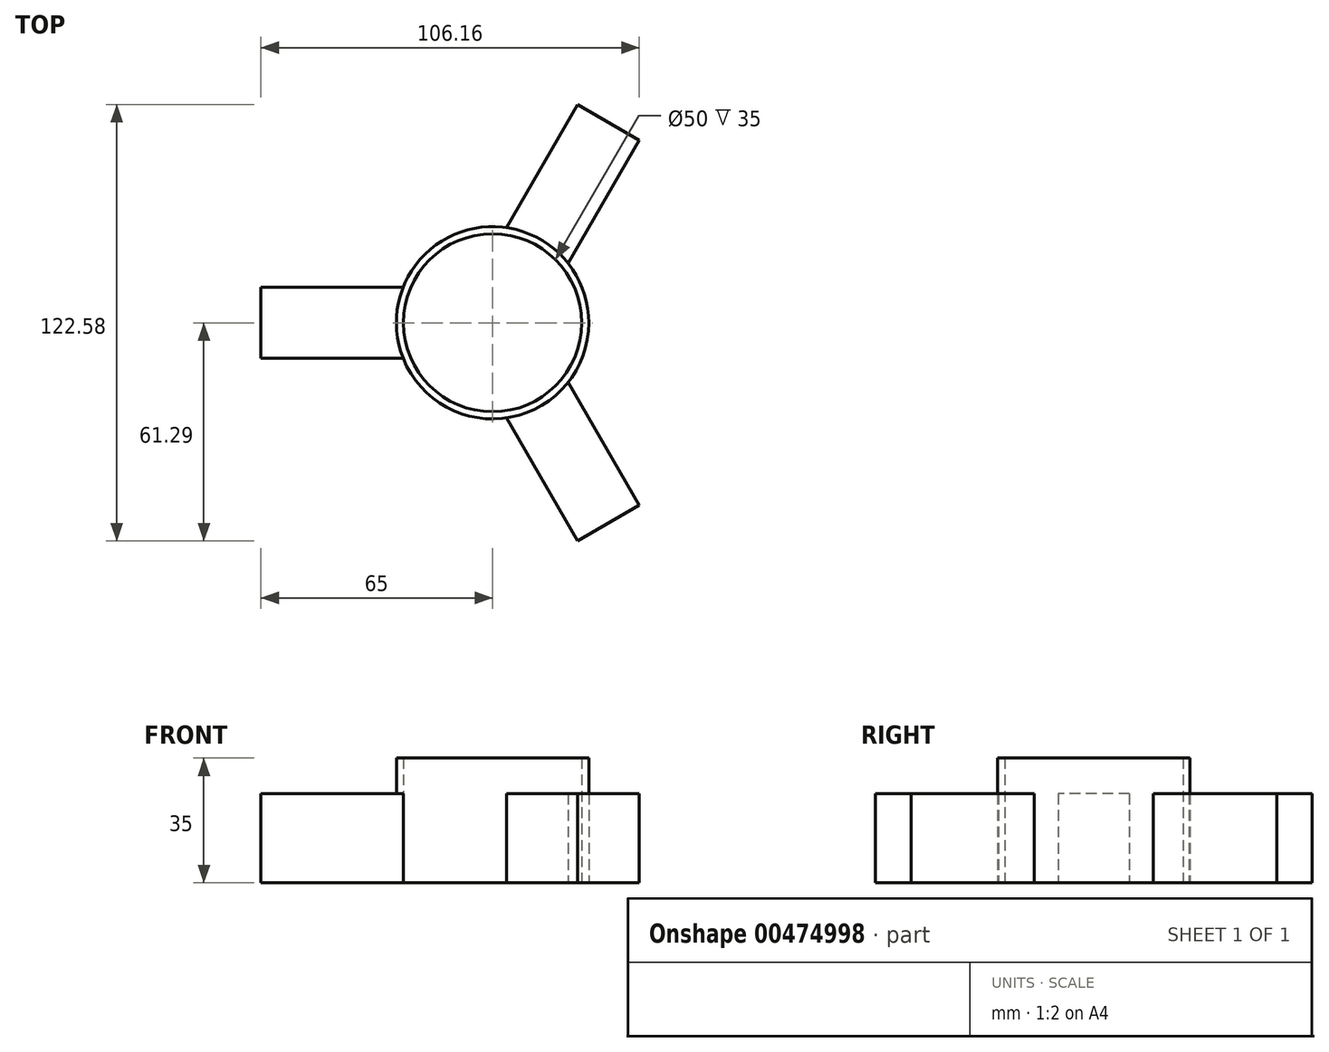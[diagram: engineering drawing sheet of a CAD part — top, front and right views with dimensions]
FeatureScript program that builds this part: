
annotation { "Feature Type Name" : "Feature", "Feature Type Description" : "" }
export const myFeature = defineFeature(function(context is Context, id is Id, definition is map)
    precondition{}
    {
        {
            var Q0;
            Q0=qCreatedBy(makeId("Top.planeOp"),FACE);
            var sketch = newSketch(context, id + "F0", { "sketchPlane" : qUnion([Q0])});
            skCircle(sketch, "E0", {"center": v(0, 0) * mm, "radius": 25 * mm});
            skCircle(sketch, "E1.0", {"center": v(0, 0) * mm, "radius": 27 * mm});
            skLineSegment(sketch, "E2.bottom", {"start": v(-65, 10) * mm, "end": v(-25, 10) * mm});
            skLineSegment(sketch, "E2.top", {"start": v(-65, -10) * mm, "end": v(-25, -10) * mm});
            skLineSegment(sketch, "E2.left", {"start": v(-65, 10) * mm, "end": v(-65, -10) * mm});
            skLineSegment(sketch, "E3.1.0", {"start": v(23.84, -61.3) * mm, "end": v(41.16, -51.3) * mm});
            skLineSegment(sketch, "E3.1.1", {"start": v(23.84, -61.3) * mm, "end": v(3.84, -26.65) * mm});
            skLineSegment(sketch, "E3.1.3", {"start": v(41.16, -51.3) * mm, "end": v(21.16, -16.65) * mm});
            skLineSegment(sketch, "E3.2.0", {"start": v(41.16, 51.3) * mm, "end": v(23.84, 61.3) * mm});
            skLineSegment(sketch, "E3.2.1", {"start": v(41.16, 51.3) * mm, "end": v(21.16, 16.65) * mm});
            skLineSegment(sketch, "E3.2.3", {"start": v(23.84, 61.3) * mm, "end": v(3.84, 26.65) * mm});
            skSolve(sketch);
        }
        {
            var Q0;
            Q0=makeQuery(id+"F0.imprint","IMPRINT",FACE,{"disambiguationData":[TD([[makeQuery(id+"F0.imprint","IMPRINT",EDGE,{"derivedFrom":sQuery(id+"F0.wireOp",EDGE,"E0")}),-1.0]])]});
            extrude(context, id + "F1", {"entities" : qUnion([Q0]), "depth" : 35 * mm});
        }
        {
            var Q0;
            {var subQ0=sQuery(id+"F0.wireOp",EDGE,"E2.left");Q0=makeQuery(id+"F0.imprint","IMPRINT",FACE,{"disambiguationData":[TD([[makeQuery(id+"F0.imprint","IMPRINT",EDGE,{"derivedFrom":subQ0}),1.0]])]});}
            var Q1;
            {var subQ0=sQuery(id+"F0.wireOp",EDGE,"E3.1.0");Q1=makeQuery(id+"F0.imprint","IMPRINT",FACE,{"disambiguationData":[TD([[makeQuery(id+"F0.imprint","IMPRINT",EDGE,{"derivedFrom":subQ0}),1.0]])]});}
            var Q2;
            {var subQ0=sQuery(id+"F0.wireOp",EDGE,"E3.2.0");Q2=makeQuery(id+"F0.imprint","IMPRINT",FACE,{"disambiguationData":[TD([[makeQuery(id+"F0.imprint","IMPRINT",EDGE,{"derivedFrom":subQ0}),1.0]])]});}
            extrude(context, id + "F2", {"entities" : qUnion([Q0, Q1, Q2]), "operationType" : NewBodyOperationType.ADD, "depth" : 25 * mm});
        }
    });
